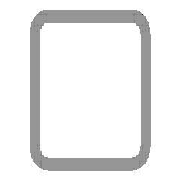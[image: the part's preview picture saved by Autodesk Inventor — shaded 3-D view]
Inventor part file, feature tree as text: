
AUTODESK INVENTOR PART (.ipt)
format: ipt  version: 2025.3 (Build 293356000, 356)  size: 134,144 bytes
history: native  units: mm (DEFAULTED — no unit token found)
features: other x4, sketch x1, plane x1
ambient origin geometry x8: Origin, YZ Plane, XZ Plane, XY Plane, X Axis, Y Axis, Z Axis, Center Point
bodies: Solid1 (feature_tree), Body (feature_tree)
feature tree (6):
  parser-record x1  (decoder bookkeeping rows leaked as tree rows — omitted from the tree; the rows remain in map.json)
  other  "Driven Length"
  other  "Start Plane"
  other  "End Plane"
  sketch  "Sketch3"  dims[d3=5400.0mm d4=0.0mm d7=6.0mm d9=80.0mm d11=80.0mm d12=3.0mm d13=-0.0mm d14=5400.0mm d15=40.0mm d16=40.0mm d17=90.0deg d18=5400.0mm]
  plane  "Work Plane3"
